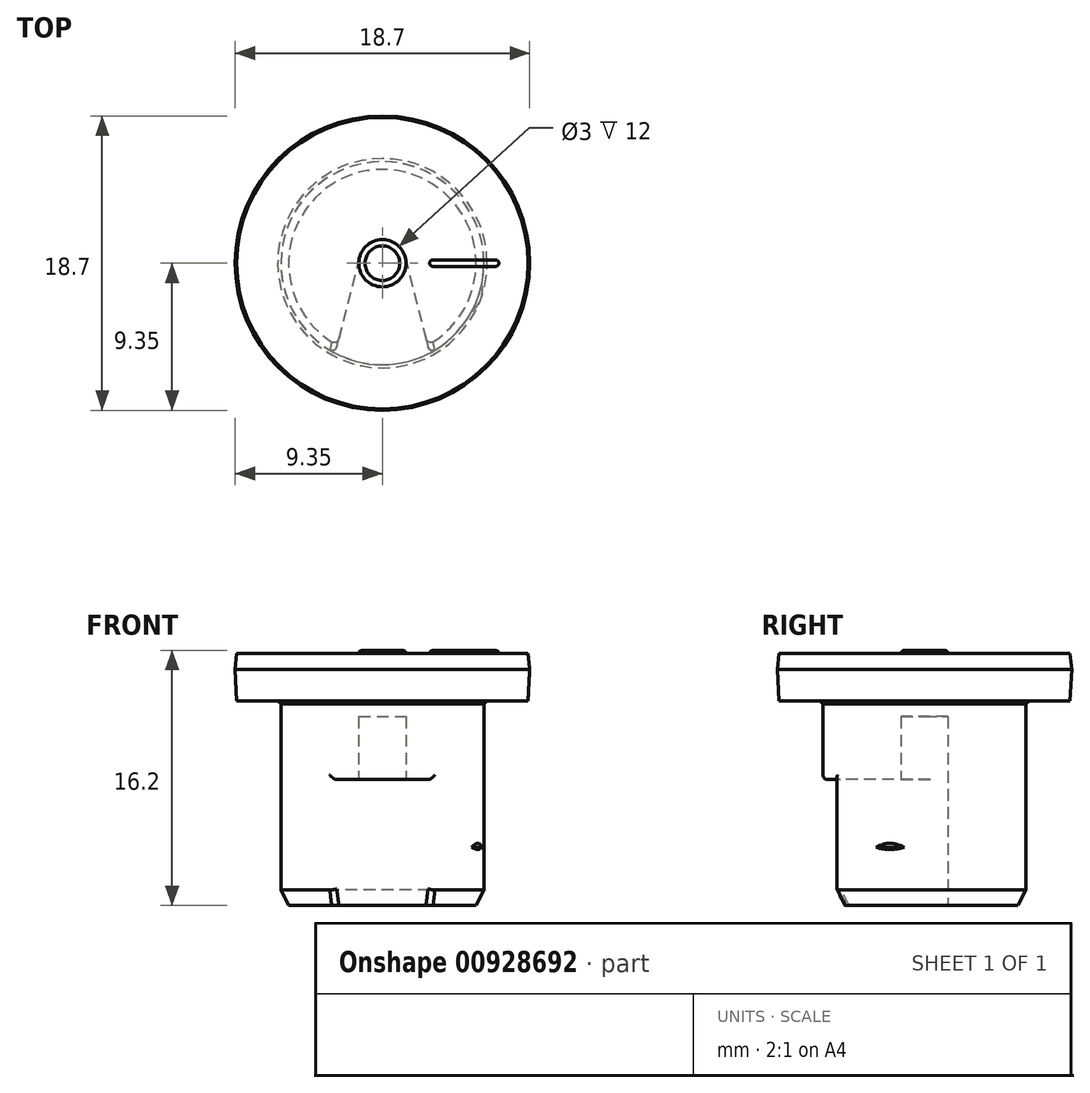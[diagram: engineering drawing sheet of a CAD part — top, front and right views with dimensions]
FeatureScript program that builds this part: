
annotation { "Feature Type Name" : "Feature", "Feature Type Description" : "" }
export const myFeature = defineFeature(function(context is Context, id is Id, definition is map)
    precondition{}
    {
        {
            var Q0;
            Q0=qCreatedBy(makeId("Front.planeOp"),FACE);
            var sketch = newSketch(context, id + "F0", { "sketchPlane" : qUnion([Q0])});
            skLineSegment(sketch, "E0", {"start": v(0, 17.95) * mm, "end": v(0, 0) * mm, "construction": true});
            skLineSegment(sketch, "E1", {"start": v(0, 0) * mm, "end": v(-5.95, 0) * mm});
            skLineSegment(sketch, "E2", {"start": v(-6.45, 1) * mm, "end": v(-6.45, 13) * mm});
            skLineSegment(sketch, "E3", {"start": v(-6.45, 13) * mm, "end": v(-9.25, 13) * mm});
            skLineSegment(sketch, "E4", {"start": v(-9.35, 15) * mm, "end": v(-9.25, 16) * mm});
            skLineSegment(sketch, "E5", {"start": v(-9.25, 16) * mm, "end": v(0, 16) * mm});
            skLineSegment(sketch, "E6", {"start": v(-9.35, 15) * mm, "end": v(-9.25, 13) * mm});
            skLineSegment(sketch, "E7", {"start": v(-6.45, 1) * mm, "end": v(-5.95, 0) * mm});
            skPoint(sketch, "E8.orphan", {"position": v(-6.45, 0) * mm});
            skLineSegment(sketch, "E9", {"start": v(0, 16) * mm, "end": v(0, 0) * mm});
            skSolve(sketch);
        }
        {
            var Q0;
            Q0=makeQuery(id+"F0.imprint","IMPRINT",FACE,{"disambiguationData":[TD([[makeQuery(id+"F0.imprint","IMPRINT",EDGE,{"derivedFrom":sQuery(id+"F0.wireOp",EDGE,"E1")}),-1.0]])]});
            var Q1;
            Q1=sQuery(id+"F0.wireOp",EDGE,"Krabe9E8-caii-Rj8K-JC3p-4sixbxrEj6TI");
            var Q2;
            Q2=sQuery(id+"F0.wireOp",EDGE,"E2");
            var Q3;
            Q3=sQuery(id+"F0.wireOp",EDGE,"0r4yqqa4-Ij3X-YIVf-rbzo-mKQMgVyfvwQ8");
            var Q4;
            Q4=sQuery(id+"F0.wireOp",EDGE,"E0");
            revolve(context, id + "F1", {"entities" : qUnion([Q0]), "surfaceEntities" : qUnion([Q1, Q2, Q3]), "axis" : qUnion([Q4]), "revolveType" : RevolveType.FULL});
        }
        {
            var Q0;
            Q0=makeQuery(id+"F1.opRevolve","SWEPT_FACE",FACE,{"disambiguationData":[OSD([sQuery(id+"F0.wireOp",EDGE,"E5")])]});
            var sketch = newSketch(context, id + "F2", { "sketchPlane" : qUnion([Q0])});
            skLineSegment(sketch, "E10.bottom", {"start": v(3.2, 0.2) * mm, "end": v(7.2, 0.2) * mm});
            skArc(sketch, "E11", {"start": v(3.2, 0.2) * mm, "mid": v(3.06, 0.14) * mm, "end": v(3, 0) * mm});
            skArc(sketch, "E12", {"start": v(7.4, 0) * mm, "mid": v(7.34, 0.14) * mm, "end": v(7.2, 0.2) * mm});
            skLineSegment(sketch, "E13", {"start": v(2.13, 0) * mm, "end": v(5.64, 0) * mm, "construction": true});
            skLineSegment(sketch, "E14", {"start": v(3, 0) * mm, "end": v(7.4, 0) * mm});
            skSolve(sketch);
        }
        {
            var Q0;
            Q0=makeQuery(id+"F2.imprint","IMPRINT",FACE,{"disambiguationData":[TD([[makeQuery(id+"F2.imprint","IMPRINT",EDGE,{"derivedFrom":sQuery(id+"F2.wireOp",EDGE,"E10.bottom")}),-1.0]])]});
            var Q1;
            Q1=sQuery(id+"F2.wireOp",EDGE,"E13");
            revolve(context, id + "F3", {"operationType" : NewBodyOperationType.ADD, "entities" : qUnion([Q0]), "axis" : qUnion([Q1]), "revolveType" : RevolveType.FULL});
        }
        {
            var Q0;
            Q0=makeQuery(id+"F1.opRevolve","SWEPT_FACE",FACE,{"disambiguationData":[OSD([sQuery(id+"F0.wireOp",EDGE,"E5")])]});
            var sketch = newSketch(context, id + "F4", { "sketchPlane" : qUnion([Q0])});
            skLineSegment(sketch, "E15", {"start": v(6.95, 0) * mm, "end": v(0, 0) * mm, "construction": true});
            skCircle(sketch, "E16", {"center": v(0, 0) * mm, "radius": 1.5 * mm});
            skCircle(sketch, "E17", {"center": v(0, 0) * mm, "radius": 1.1 * mm});
            skSolve(sketch);
        }
        {
            var Q0;
            Q0=makeQuery(id+"F4.imprint","IMPRINT",FACE,{"disambiguationData":[TD([[makeQuery(id+"F4.imprint","IMPRINT",EDGE,{"derivedFrom":sQuery(id+"F4.wireOp",EDGE,"E16")}),1.0]])]});
            extrude(context, id + "F5", {"entities" : qUnion([Q0]), "operationType" : NewBodyOperationType.ADD, "offsetDistance" : 25 * mm, "depth" : .2 * mm});
        }
        {
            var Q0;
            Q0=makeQuery(id+"F5.opExtrude","CAP_FACE",FACE,{"disambiguationData":[OSD([sQuery(id+"F4.wireOp",EDGE,"E16"),sQuery(id+"F4.wireOp",EDGE,"E17")])],"isStart":false});
            fillet(context, id + "F6", {"entities" : qUnion([Q0]), "radius" : .2 * mm, "tangentPropagation" : true, "allowEdgeOverflow" : false});
        }
        {
            var Q0;
            Q0=makeQuery(id+"F1.opRevolve","SWEPT_FACE",FACE,{"disambiguationData":[OSD([sQuery(id+"F0.wireOp",EDGE,"E1")])]});
            var sketch = newSketch(context, id + "F7", { "sketchPlane" : qUnion([Q0])});
            skLineSegment(sketch, "E18", {"start": v(0, -9.6) * mm, "end": v(0, 9.85) * mm, "construction": true});
            skCircle(sketch, "E19", {"center": v(0, 0) * mm, "radius": 1.5 * mm});
            skLineSegment(sketch, "E20", {"start": v(-3, 5.7) * mm, "end": v(3, 5.7) * mm, "construction": true});
            skLineSegment(sketch, "E21", {"start": v(1.45, -0.37) * mm, "end": v(4.07, 9.93) * mm});
            skLineSegment(sketch, "E22.MirrorCS", {"start": v(-1.45, -0.37) * mm, "end": v(-4.07, 9.93) * mm});
            skLineSegment(sketch, "E23", {"start": v(-4.07, 9.93) * mm, "end": v(4.07, 9.93) * mm});
            skSolve(sketch);
        }
        {
            var Q0;
            {var subQ0=sQuery(id+"F7.wireOp",EDGE,"E19");var subQ1=makeQuery(id+"F7.imprint","INTERSECT",VERTEX,{"derivedFrom":[subQ0,sQuery(id+"F7.wireOp",EDGE,"E21")]});Q0=makeQuery(id+"F7.imprint","IMPRINT",FACE,{"disambiguationData":[TD([[makeQuery(id+"F7.imprint","IMPRINT",EDGE,{"disambiguationData":[TD([[subQ1,1.0]])],"derivedFrom":subQ0}),1.0]])]});}
            var Q1;
            {var subQ0=sQuery(id+"F7.wireOp",EDGE,"E21");var subQ1=sQuery(id+"F7.wireOp",EDGE,"E19");var subQ2=makeQuery(id+"F7.imprint","INTERSECT",VERTEX,{"derivedFrom":[subQ1,subQ0]});Q1=makeQuery(id+"F7.imprint","IMPRINT",FACE,{"disambiguationData":[TD([[makeQuery(id+"F7.imprint","IMPRINT",EDGE,{"disambiguationData":[TD([[subQ2,-1.0]])],"derivedFrom":subQ1}),-1.0]])]});}
            var Q2;
            {var subQ0=sQuery(id+"F7.wireOp",EDGE,"E23");Q2=makeQuery(id+"F7.imprint","IMPRINT",FACE,{"disambiguationData":[TD([[makeQuery(id+"F7.imprint","IMPRINT",EDGE,{"derivedFrom":subQ0}),-1.0]])]});}
            var Q3;
            Q3=sQuery(id+"F7.wireOp",EDGE,"Ofkggj9q-fOiX-afXJ-uq58-gjdl14K4oSr4");
            extrude(context, id + "F8", {"entities" : qUnion([Q0, Q1, Q2]), "operationType" : NewBodyOperationType.REMOVE, "surfaceEntities" : qUnion([Q3]), "oppositeDirection" : true, "offsetDistance" : 25 * mm, "depth" : 8 * mm});
        }
        {
            var Q0;
            Q0=qCreatedBy(makeId("Top.planeOp"),FACE);
            cPlane(context, id + "F9", {"entities" : qUnion([Q0]), "cplaneType" : CPlaneType.OFFSET, "offset" : 3.7 * mm, "width" : 150 * mm, "height" : 150 * mm});
        }
        {
            var Q0;
            Q0=qCreatedBy(id+"F9.planeOp",FACE);
            var sketch = newSketch(context, id + "F10", { "sketchPlane" : qUnion([Q0])});
            skLineSegment(sketch, "E24", {"start": v(-7.22, 2.63) * mm, "end": v(8.3, -3.02) * mm, "construction": true});
            skLineSegment(sketch, "E25", {"start": v(-7.37, -2.68) * mm, "end": v(8.39, 3.05) * mm, "construction": true});
            skLineSegment(sketch, "E26", {"start": v(-9.7, 0) * mm, "end": v(10.27, 0) * mm, "construction": true});
            skArc(sketch, "E27.0", {"start": v(5.67, -3.08) * mm, "mid": v(6.06, -2.2) * mm, "end": v(6.32, -1.29) * mm});
            skArc(sketch, "E28", {"start": v(5.67, -3.08) * mm, "mid": v(6.25, -2.28) * mm, "end": v(6.32, -1.29) * mm});
            skPoint(sketch, "E29.orphan", {"position": v(3, -5.7) * mm});
            skArc(sketch, "E30.trimOffspring", {"start": v(6.06, 2.2) * mm, "mid": v(-6.02, 2.33) * mm, "end": v(3, -5.7) * mm});
            skSolve(sketch);
        }
        {
            var Q0;
            {var subQ0=sQuery(id+"F10.wireOp",EDGE,"E28");Q0=makeQuery(id+"F10.imprint","IMPRINT",FACE,{"disambiguationData":[TD([[makeQuery(id+"F10.imprint","IMPRINT",EDGE,{"derivedFrom":subQ0}),1.0]])]});}
            var Q1;
            {var subQ0=sQuery(id+"F10.wireOp",EDGE,"807161e0-a8de-460d-b0ac-e282d0f2d88c0.MirrorCS");Q1=makeQuery(id+"F10.imprint","IMPRINT",FACE,{"disambiguationData":[TD([[makeQuery(id+"F10.imprint","IMPRINT",EDGE,{"derivedFrom":subQ0}),-1.0]])]});}
            extrude(context, id + "F11", {"entities" : qUnion([Q0, Q1]), "operationType" : NewBodyOperationType.ADD, "depth" : .25 * mm, "hasSecondDirection" : true, "secondDirectionOppositeDirection" : true, "secondDirectionDepth" : .20 * mm});
        }
        {
            var Q0;
            Q0=makeQuery(id+"F11.opExtrude","CAP_EDGE",EDGE,{"disambiguationData":[OSD([sQuery(id+"F10.wireOp",EDGE,"E28")])],"isStart":false});
            var Q1;
            Q1=makeQuery(id+"FwXyqYgep1eXdiE_1.1.F11.opExtrude","CAP_EDGE",EDGE,{"disambiguationData":[OSD([sQuery(id+"F10.wireOp",EDGE,"807161e0-a8de-460d-b0ac-e282d0f2d88c0.MirrorCS")])],"isStart":false});
            chamfer(context, id + "F12", {"entities" : qUnion([Q0, Q1]), "chamferType" : ChamferType.TWO_OFFSETS, "width1" : .205 * mm, "oppositeDirection" : false, "width2" : .25 * mm, "tangentPropagation" : true});
        }
        {
            var Q0;
            Q0=makeQuery(id+"F11.opExtrude","CAP_EDGE",EDGE,{"disambiguationData":[OSD([sQuery(id+"F10.wireOp",EDGE,"E28")])],"isStart":true});
            var Q1;
            Q1=makeQuery(id+"FwXyqYgep1eXdiE_1.1.F11.opExtrude","CAP_EDGE",EDGE,{"disambiguationData":[OSD([sQuery(id+"F10.wireOp",EDGE,"807161e0-a8de-460d-b0ac-e282d0f2d88c0.MirrorCS")])],"isStart":true});
            chamfer(context, id + "F13", {"entities" : qUnion([Q0, Q1]), "chamferType" : ChamferType.TWO_OFFSETS, "width1" : .2 * mm, "oppositeDirection" : false, "width2" : .3 * mm, "tangentPropagation" : true});
        }
        {
            var Q0;
            Q0=makeQuery(id+"F1.opRevolve","SWEPT_EDGE",EDGE,{"disambiguationData":[OSD([sQuery(id+"F0.wireOp",EDGE,"E2"),sQuery(id+"F0.wireOp",EDGE,"E3")])]});
            chamfer(context, id + "F14", {"entities" : qUnion([Q0]), "width" : .2 * mm, "tangentPropagation" : true});
        }
        {
            var Q0;
            {var subQ0=sQuery(id+"F7.wireOp",EDGE,"E19");var subQ1=makeQuery(id+"F7.imprint","INTERSECT",VERTEX,{"derivedFrom":[subQ0,sQuery(id+"F7.wireOp",EDGE,"E21")]});Q0=makeQuery(id+"F7.imprint","IMPRINT",FACE,{"disambiguationData":[TD([[makeQuery(id+"F7.imprint","IMPRINT",EDGE,{"disambiguationData":[TD([[subQ1,1.0]])],"derivedFrom":subQ0}),1.0]])]});}
            extrude(context, id + "F15", {"entities" : qUnion([Q0]), "operationType" : NewBodyOperationType.REMOVE, "oppositeDirection" : true, "depth" : 12 * mm, "offsetDistance" : 25 * mm});
        }
        {
            var Q0;
            Q0=makeQuery(id+"F8.boolean.opBoolean","INTERSECT",EDGE,{"derivedFrom":[makeQuery(id+"F1.opRevolve","SWEPT_FACE",FACE,{"disambiguationData":[OSD([sQuery(id+"F0.wireOp",EDGE,"E2")])]}),makeQuery(id+"F8.opExtrude","SWEPT_FACE",FACE,{"disambiguationData":[OSD([sQuery(id+"F7.wireOp",EDGE,"E22.MirrorCS")])]})]});
            var Q1;
            Q1=makeQuery(id+"F8.boolean.opBoolean","INTERSECT",EDGE,{"derivedFrom":[makeQuery(id+"F1.opRevolve","SWEPT_FACE",FACE,{"disambiguationData":[OSD([sQuery(id+"F0.wireOp",EDGE,"E2")])]}),makeQuery(id+"F8.opExtrude","CAP_FACE",FACE,{"disambiguationData":[OSD([sQuery(id+"F7.wireOp",EDGE,"E19"),sQuery(id+"F7.wireOp",EDGE,"E21"),sQuery(id+"F7.wireOp",EDGE,"E22.MirrorCS"),sQuery(id+"F7.wireOp",EDGE,"E23")])],"isStart":false})]});
            var Q2;
            Q2=makeQuery(id+"F8.boolean.opBoolean","INTERSECT",EDGE,{"derivedFrom":[makeQuery(id+"F1.opRevolve","SWEPT_FACE",FACE,{"disambiguationData":[OSD([sQuery(id+"F0.wireOp",EDGE,"E2")])]}),makeQuery(id+"F8.opExtrude","SWEPT_FACE",FACE,{"disambiguationData":[OSD([sQuery(id+"F7.wireOp",EDGE,"E21")])]})]});
            var Q3;
            Q3=makeQuery(id+"F8.boolean.opBoolean","INTERSECT",EDGE,{"derivedFrom":[makeQuery(id+"F1.opRevolve","SWEPT_FACE",FACE,{"disambiguationData":[OSD([sQuery(id+"F0.wireOp",EDGE,"E7")])]}),makeQuery(id+"F8.opExtrude","SWEPT_FACE",FACE,{"disambiguationData":[OSD([sQuery(id+"F7.wireOp",EDGE,"E21")])]})]});
            var Q4;
            Q4=makeQuery(id+"F8.boolean.opBoolean","INTERSECT",EDGE,{"derivedFrom":[makeQuery(id+"F1.opRevolve","SWEPT_FACE",FACE,{"disambiguationData":[OSD([sQuery(id+"F0.wireOp",EDGE,"E7")])]}),makeQuery(id+"F8.opExtrude","SWEPT_FACE",FACE,{"disambiguationData":[OSD([sQuery(id+"F7.wireOp",EDGE,"E22.MirrorCS")])]})]});
            fillet(context, id + "F16", {"entities" : qUnion([Q0, Q1, Q2, Q3, Q4]), "radius" : .3 * mm, "tangentPropagation" : true, "allowEdgeOverflow" : false});
        }
    });
